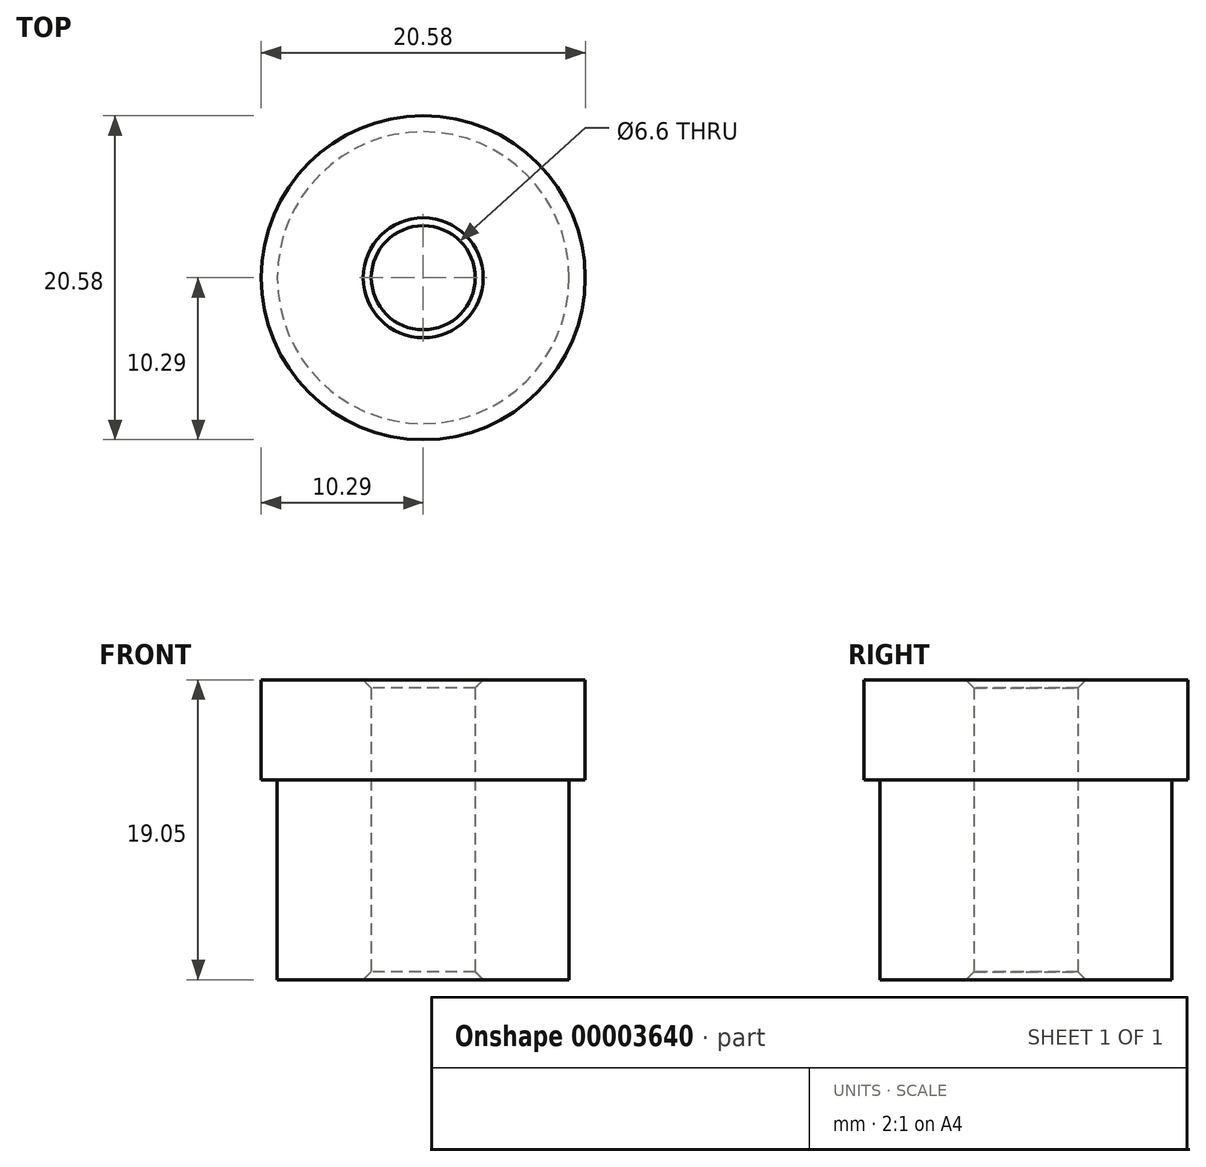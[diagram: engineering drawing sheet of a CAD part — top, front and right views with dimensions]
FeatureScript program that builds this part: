
annotation { "Feature Type Name" : "Feature", "Feature Type Description" : "" }
export const myFeature = defineFeature(function(context is Context, id is Id, definition is map)
    precondition{}
    {
        {
            var Q0;
            Q0=qCreatedBy(makeId("Top.planeOp"),FACE);
            var sketch = newSketch(context, id + "F0", { "sketchPlane" : qUnion([Q0])});
            skCircle(sketch, "E0", {"center": v(0, 0) * mm, "radius": 10.29 * mm});
            skCircle(sketch, "E1", {"center": v(0, 0) * mm, "radius": 3.3 * mm});
            skSolve(sketch);
        }
        {
            var Q0;
            Q0=qSketchRegion(id+"F0",true);
            extrude(context, id + "F1", {"entities" : qUnion([Q0]), "depth" : 19.05 * mm});
        }
        {
            var Q0;
            Q0=makeQuery(id+"F1.opExtrude","CAP_FACE",FACE,{"disambiguationData":[OSD([sQuery(id+"F0.wireOp",EDGE,"E0"),sQuery(id+"F0.wireOp",EDGE,"E1")])],"isStart":true});
            var sketch = newSketch(context, id + "F2", { "sketchPlane" : qUnion([Q0])});
            skCircle(sketch, "E2", {"center": v(0, 0) * mm, "radius": 9.27 * mm});
            skCircle(sketch, "E3.0", {"center": v(0, 0) * mm, "radius": 10.29 * mm});
            skSolve(sketch);
        }
        {
            var Q0;
            Q0=makeQuery(id+"F2.imprint","IMPRINT",FACE,{"disambiguationData":[TD([[makeQuery(id+"F2.imprint","IMPRINT",EDGE,{"derivedFrom":sQuery(id+"F2.wireOp",EDGE,"E2")}),-1.0]])]});
            extrude(context, id + "F3", {"entities" : qUnion([Q0]), "operationType" : NewBodyOperationType.REMOVE, "oppositeDirection" : true, "depth" : 12.7 * mm});
        }
        {
            var Q0;
            Q0=makeQuery(id+"F1.opExtrude","CAP_FACE",FACE,{"disambiguationData":[OSD([sQuery(id+"F0.wireOp",EDGE,"E0"),sQuery(id+"F0.wireOp",EDGE,"E1")])],"isStart":false});
            var sketch = newSketch(context, id + "F4", { "sketchPlane" : qUnion([Q0])});
            skCircle(sketch, "E4", {"center": v(0, 0) * mm, "radius": 5.97 * mm});
            skCircle(sketch, "E5.0", {"center": v(0, 0) * mm, "radius": 3.3 * mm});
            skSolve(sketch);
        }
        {
            var Q0;
            Q0=makeQuery(id+"F1.opExtrude","CAP_EDGE",EDGE,{"disambiguationData":[OSD([sQuery(id+"F0.wireOp",EDGE,"E1")])],"isStart":true});
            var Q1;
            Q1=makeQuery(id+"F1.opExtrude","CAP_EDGE",EDGE,{"disambiguationData":[OSD([sQuery(id+"F0.wireOp",EDGE,"E1")])],"isStart":false});
            chamfer(context, id + "F5", {"entities" : qUnion([Q0, Q1]), "width" : 0.5 * mm, "tangentPropagation" : true});
        }
    });
